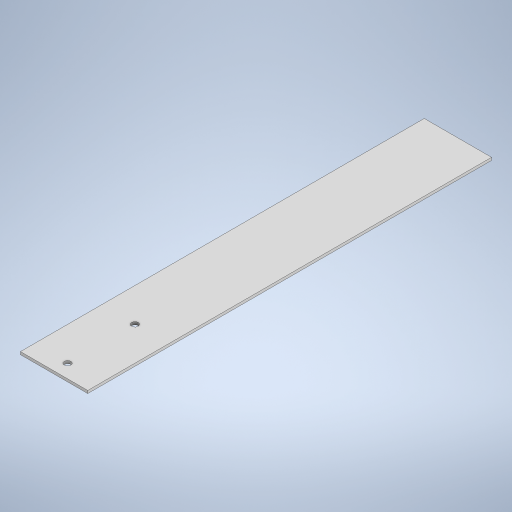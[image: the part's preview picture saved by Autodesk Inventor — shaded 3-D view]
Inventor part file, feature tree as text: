
AUTODESK INVENTOR PART (.ipt)
format: ipt  version: 2023 (Build 270158000, 158)  size: 229,376 bytes
history: native  units: mm
features: extrude x1, sketch x1
ambient origin geometry x8: Origin, YZ Plane, XZ Plane, XY Plane, X Axis, Y Axis, Z Axis, Center Point
bodies: Solid1 (feature_tree)
feature tree (2):
  extrude  "Extrusion1"  Depth=300.0mm
  sketch  "Sketch1"  dims[d0=50.0mm d1=300.0mm d2=10.0mm d3=5.0mm d4=50.0mm d5=5.0mm d6=2.0mm d7=0.0mm]
